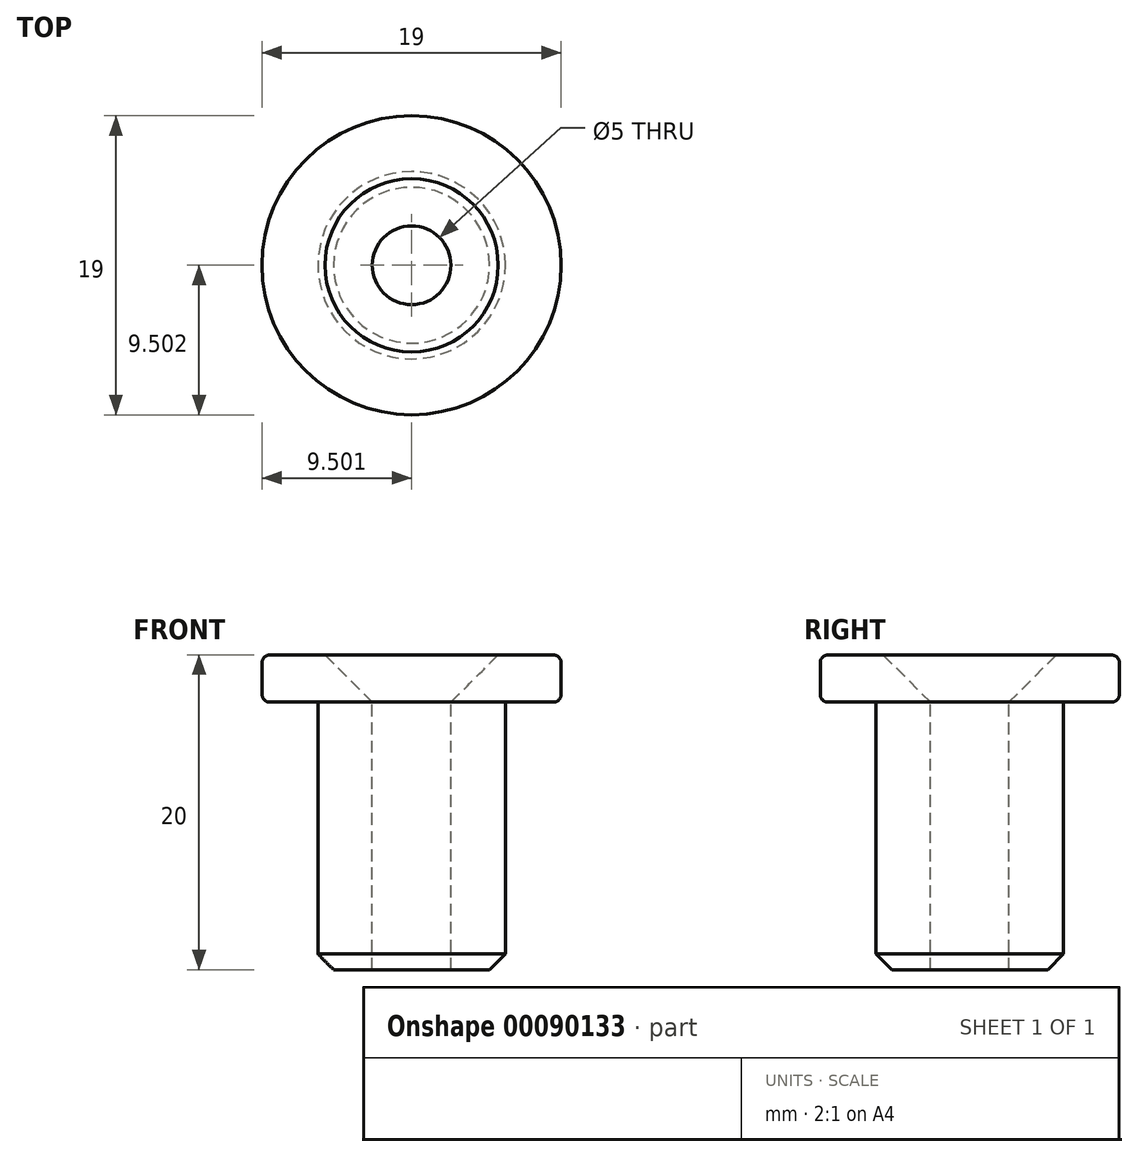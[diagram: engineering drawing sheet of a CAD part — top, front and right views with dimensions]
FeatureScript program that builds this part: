
annotation { "Feature Type Name" : "Feature", "Feature Type Description" : "" }
export const myFeature = defineFeature(function(context is Context, id is Id, definition is map)
    precondition{}
    {
        {
            var Q0;
            Q0=qCreatedBy(makeId("Top.planeOp"),FACE);
            var sketch = newSketch(context, id + "F0", { "sketchPlane" : qUnion([Q0])});
            skCircle(sketch, "E0", {"center": v(-18.36, 16.74) * mm, "radius": 2.5 * mm});
            skCircle(sketch, "E1", {"center": v(-18.36, 16.74) * mm, "radius": 9.5 * mm});
            skSolve(sketch);
        }
        {
            var Q0;
            Q0=makeQuery(id+"F0.imprint","IMPRINT",FACE,{"disambiguationData":[TD([[makeQuery(id+"F0.imprint","IMPRINT",EDGE,{"derivedFrom":sQuery(id+"F0.wireOp",EDGE,"E0")}),-1.0]])]});
            var Q1;
            Q1=makeQuery(id+"F0.imprint","IMPRINT",FACE,{"disambiguationData":[TD([[makeQuery(id+"F0.imprint","IMPRINT",EDGE,{"derivedFrom":sQuery(id+"F0.wireOp",EDGE,"ZX0XpBDP-Pdd1-kTLb-qjJs-TXxntM3EtFEy")}),-1.0]])]});
            var Q2;
            Q2=makeQuery(id+"F0.imprint","IMPRINT",FACE,{"disambiguationData":[TD([[makeQuery(id+"F0.imprint","IMPRINT",EDGE,{"derivedFrom":sQuery(id+"F0.wireOp",EDGE,"nmKGcCXq-oBb7-QOPK-XQJl-Q72ml5hH5Vhk")}),-1.0]])]});
            var Q3;
            Q3=makeQuery(id+"F0.imprint","IMPRINT",FACE,{"disambiguationData":[TD([[makeQuery(id+"F0.imprint","IMPRINT",EDGE,{"derivedFrom":sQuery(id+"F0.wireOp",EDGE,"6CWFLD51-ruXM-IE0f-LYmz-ql4kMtAmHs9A")}),-1.0]])]});
            extrude(context, id + "F1", {"entities" : qUnion([Q0, Q1, Q2, Q3]), "depth" : 3 * mm});
        }
        {
            var Q0;
            Q0=makeQuery(id+"F1.opExtrude","CAP_EDGE",EDGE,{"disambiguationData":[OSD([sQuery(id+"F0.wireOp",EDGE,"E0")])],"isStart":false});
            chamfer(context, id + "F2", {"entities" : qUnion([Q0]), "width" : 3 * mm, "tangentPropagation" : true});
        }
        {
            var Q0;
            Q0=makeQuery(id+"F1.opExtrude","CAP_FACE",FACE,{"disambiguationData":[OSD([sQuery(id+"F0.wireOp",EDGE,"E0"),sQuery(id+"F0.wireOp",EDGE,"E1")])],"isStart":true});
            var sketch = newSketch(context, id + "F3", { "sketchPlane" : qUnion([Q0])});
            skCircle(sketch, "E2.0", {"center": v(-18.36, -16.74) * mm, "radius": 2.5 * mm});
            skCircle(sketch, "E3", {"center": v(-18.36, -16.74) * mm, "radius": 5.95 * mm});
            skSolve(sketch);
        }
        {
            var Q0;
            Q0=makeQuery(id+"F3.imprint","IMPRINT",FACE,{"disambiguationData":[TD([[makeQuery(id+"F3.imprint","IMPRINT",EDGE,{"derivedFrom":sQuery(id+"F3.wireOp",EDGE,"E2.0")}),1.0]])]});
            extrude(context, id + "F4", {"entities" : qUnion([Q0]), "operationType" : NewBodyOperationType.ADD, "depth" : 17 * mm});
        }
        {
            var Q0;
            Q0=makeQuery(id+"F4.opExtrude","CAP_EDGE",EDGE,{"disambiguationData":[OSD([sQuery(id+"F3.wireOp",EDGE,"E3")])],"isStart":false});
            chamfer(context, id + "F5", {"entities" : qUnion([Q0]), "width" : 1 * mm, "tangentPropagation" : true});
        }
        {
            var Q0;
            Q0=makeQuery(id+"F1.opExtrude","CAP_EDGE",EDGE,{"disambiguationData":[OSD([sQuery(id+"F0.wireOp",EDGE,"E1")])],"isStart":true});
            var Q1;
            Q1=makeQuery(id+"F1.opExtrude","CAP_EDGE",EDGE,{"disambiguationData":[OSD([sQuery(id+"F0.wireOp",EDGE,"E1")])],"isStart":false});
            var Q2;
            Q2=makeQuery(id+"F4.opExtrude","CAP_EDGE",EDGE,{"disambiguationData":[OSD([sQuery(id+"F3.wireOp",EDGE,"E3")])],"isStart":true});
            fillet(context, id + "F6", {"entities" : qUnion([Q0, Q1, Q2]), "radius" : .5 * mm, "tangentPropagation" : true, "allowEdgeOverflow" : false});
        }
    });
